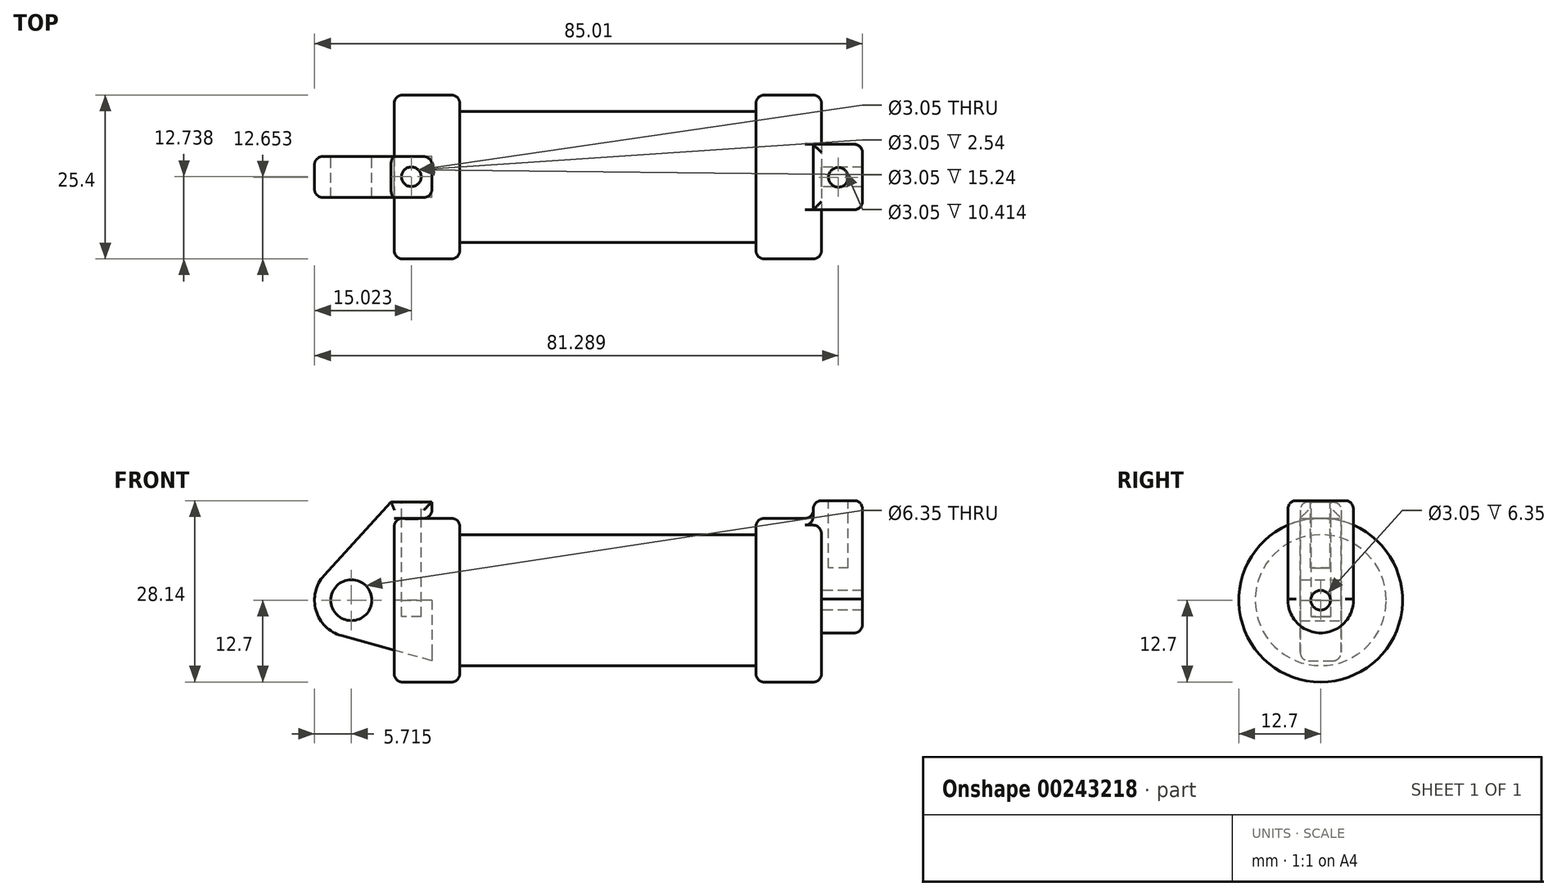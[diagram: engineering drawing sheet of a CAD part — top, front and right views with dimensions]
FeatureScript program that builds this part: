
annotation { "Feature Type Name" : "Feature", "Feature Type Description" : "" }
export const myFeature = defineFeature(function(context is Context, id is Id, definition is map)
    precondition{}
    {
        {
            var Q0;
            Q0=qCreatedBy(makeId("Front.planeOp"),FACE);
            var sketch = newSketch(context, id + "F0", { "sketchPlane" : qUnion([Q0])});
            skLineSegment(sketch, "E0", {"start": v(0, 0) * mm, "end": v(0, 12.7) * mm});
            skLineSegment(sketch, "E1", {"start": v(0, 12.7) * mm, "end": v(10.16, 12.7) * mm});
            skLineSegment(sketch, "E2", {"start": v(10.16, 12.7) * mm, "end": v(10.16, 10.16) * mm});
            skLineSegment(sketch, "E3", {"start": v(10.16, 10.16) * mm, "end": v(56.13, 10.16) * mm});
            skLineSegment(sketch, "E4", {"start": v(56.13, 10.16) * mm, "end": v(56.13, 12.7) * mm});
            skLineSegment(sketch, "E5", {"start": v(56.13, 12.7) * mm, "end": v(66.3, 12.7) * mm});
            skLineSegment(sketch, "E6", {"start": v(66.3, 12.7) * mm, "end": v(66.3, 0) * mm});
            skLineSegment(sketch, "E7", {"start": v(66.3, 0) * mm, "end": v(0, 0) * mm});
            skLineSegment(sketch, "E8", {"start": v(5.84, 15.24) * mm, "end": v(-0.5, 15.24) * mm});
            skLineSegment(sketch, "E9", {"start": v(-0.5, 15.24) * mm, "end": v(-10.88, 3.85) * mm});
            skLineSegment(sketch, "E10", {"start": v(0, 0) * mm, "end": v(-6.65, 0) * mm});
            skCircle(sketch, "E11", {"center": v(-6.65, 0) * mm, "radius": 5.72 * mm});
            skCircle(sketch, "E12", {"center": v(-6.65, 0) * mm, "radius": 3.18 * mm});
            skLineSegment(sketch, "E13", {"start": v(5.84, 15.24) * mm, "end": v(5.84, -9.4) * mm});
            skLineSegment(sketch, "E14", {"start": v(5.84, -9.4) * mm, "end": v(-8.18, -5.5) * mm});
            skSolve(sketch);
        }
        {
            var Q0;
            {var subQ0=sQuery(id+"F0.wireOp",EDGE,"E0");Q0=makeQuery(id+"F0.imprint","IMPRINT",FACE,{"disambiguationData":[TD([[makeQuery(id+"F0.imprint","IMPRINT",EDGE,{"derivedFrom":subQ0}),-1.0]])]});}
            var Q1;
            {var subQ0=sQuery(id+"F0.wireOp",EDGE,"E2");Q1=makeQuery(id+"F0.imprint","IMPRINT",FACE,{"disambiguationData":[TD([[makeQuery(id+"F0.imprint","IMPRINT",EDGE,{"derivedFrom":subQ0}),-1.0]])]});}
            var Q2;
            Q2=sQuery(id+"F0.wireOp",EDGE,"E7");
            revolve(context, id + "F1", {"entities" : qUnion([Q0, Q1]), "axis" : qUnion([Q2]), "revolveType" : RevolveType.FULL});
        }
        {
            var Q0;
            {var subQ3=sQuery(id+"F0.wireOp",EDGE,"E0");Q0=makeQuery(id+"F0.imprint","IMPRINT",FACE,{"disambiguationData":[TD([[makeQuery(id+"F0.imprint","IMPRINT",EDGE,{"derivedFrom":subQ3}),1.0]])]});}
            var Q1;
            {var subQ4=sQuery(id+"F0.wireOp",EDGE,"E12");Q1=makeQuery(id+"F0.imprint","IMPRINT",FACE,{"disambiguationData":[TD([[makeQuery(id+"F0.imprint","IMPRINT",EDGE,{"derivedFrom":subQ4}),-1.0]])]});}
            var Q2;
            {var subQ0=sQuery(id+"F0.wireOp",EDGE,"E14");Q2=makeQuery(id+"F0.imprint","IMPRINT",FACE,{"disambiguationData":[TD([[makeQuery(id+"F0.imprint","IMPRINT",EDGE,{"derivedFrom":subQ0}),-1.0]])]});}
            extrude(context, id + "F2", {"entities" : qUnion([Q0, Q1, Q2]), "endBound" : BoundingType.SYMMETRIC, "depth" : 6.35 * mm});
        }
        {
            var Q0;
            Q0=makeQuery(id+"F1.opRevolve","SWEPT_FACE",FACE,{"disambiguationData":[OSD([sQuery(id+"F0.wireOp",EDGE,"E6")])]});
            var sketch = newSketch(context, id + "F3", { "sketchPlane" : qUnion([Q0])});
            skCircle(sketch, "E15", {"center": v(0, 0) * mm, "radius": 1.52 * mm});
            skCircle(sketch, "E16", {"center": v(0, 0) * mm, "radius": 5.08 * mm});
            skLineSegment(sketch, "E17", {"start": v(-5.08, 0.2) * mm, "end": v(-5.08, 15.44) * mm});
            skLineSegment(sketch, "E18.MirrorCS", {"start": v(5.08, 0.2) * mm, "end": v(5.08, 15.44) * mm});
            skLineSegment(sketch, "E19", {"start": v(-5.08, 15.44) * mm, "end": v(5.19, 15.44) * mm});
            skSolve(sketch);
        }
        {
            var Q0;
            {var subQ0=sQuery(id+"F3.wireOp",EDGE,"E19");var subQ1=sQuery(id+"F3.wireOp",EDGE,"E17");var subQ2=makeQuery(id+"F3.imprint","INTERSECT",VERTEX,{"derivedFrom":[subQ1,subQ0]});Q0=makeQuery(id+"F3.imprint","IMPRINT",FACE,{"disambiguationData":[TD([[makeQuery(id+"F3.imprint","IMPRINT",EDGE,{"disambiguationData":[TD([[subQ2,-1.0]])],"derivedFrom":subQ0}),-1.0]])]});}
            var Q1;
            {var subQ0=sQuery(id+"F3.wireOp",EDGE,"E17");var subQ1=sQuery(id+"F3.wireOp",EDGE,"E16");var subQ2=makeQuery(id+"F3.imprint","INTERSECT",VERTEX,{"derivedFrom":[subQ1,subQ0]});Q1=makeQuery(id+"F3.imprint","IMPRINT",FACE,{"disambiguationData":[TD([[makeQuery(id+"F3.imprint","IMPRINT",EDGE,{"disambiguationData":[TD([[subQ2,1.0]])],"derivedFrom":subQ1}),-1.0]])]});}
            var Q2;
            Q2=makeQuery(id+"F3.imprint","IMPRINT",FACE,{"disambiguationData":[TD([[makeQuery(id+"F3.imprint","IMPRINT",EDGE,{"derivedFrom":sQuery(id+"F3.wireOp",EDGE,"E15")}),-1.0]])]});
            extrude(context, id + "F4", {"entities" : qUnion([Q0, Q1, Q2]), "operationType" : NewBodyOperationType.ADD, "depth" : 6.35 * mm, "hasSecondDirection" : true, "secondDirectionOppositeDirection" : true, "secondDirectionDepth" : 1.27 * mm});
        }
        {
            var Q0;
            Q0=makeQuery(id+"F2.opExtrude","SWEPT_FACE",FACE,{"disambiguationData":[OSD([sQuery(id+"F0.wireOp",EDGE,"E8")])]});
            var sketch = newSketch(context, id + "F5", { "sketchPlane" : qUnion([Q0])});
            skCircle(sketch, "E20", {"center": v(2.65, 0.04) * mm, "radius": 1.52 * mm});
            skCircle(sketch, "E21", {"center": v(68.87, 0.04) * mm, "radius": 1.52 * mm});
            skSolve(sketch);
        }
        {
            var Q0;
            Q0=makeQuery(id+"F5.imprint","IMPRINT",FACE,{"disambiguationData":[TD([[makeQuery(id+"F5.imprint","IMPRINT",EDGE,{"derivedFrom":sQuery(id+"F5.wireOp",EDGE,"E20")}),1.0]])]});
            extrude(context, id + "F6", {"entities" : qUnion([Q0]), "operationType" : NewBodyOperationType.REMOVE, "oppositeDirection" : true, "depth" : 17.78 * mm});
        }
        {
            var Q0;
            Q0=makeQuery(id+"F4.opExtrude","SWEPT_FACE",FACE,{"disambiguationData":[OSD([sQuery(id+"F3.wireOp",EDGE,"E19")])]});
            var sketch = newSketch(context, id + "F7", { "sketchPlane" : qUnion([Q0])});
            skCircle(sketch, "E22", {"center": v(68.92, -0.05) * mm, "radius": 1.52 * mm});
            skSolve(sketch);
        }
        {
            var Q0;
            Q0=makeQuery(id+"F7.imprint","IMPRINT",FACE,{"disambiguationData":[TD([[makeQuery(id+"F7.imprint","IMPRINT",EDGE,{"derivedFrom":sQuery(id+"F7.wireOp",EDGE,"E22")}),1.0]])]});
            extrude(context, id + "F8", {"entities" : qUnion([Q0]), "operationType" : NewBodyOperationType.REMOVE, "oppositeDirection" : true, "depth" : 10.4 * mm});
        }
        {
            var Q0;
            Q0=makeQuery(id+"F4.opExtrude","CAP_EDGE",EDGE,{"disambiguationData":[OSD([sQuery(id+"F3.wireOp",EDGE,"E19")])],"isStart":false});
            var Q1;
            Q1=makeQuery(id+"F4.opExtrude","CAP_EDGE",EDGE,{"disambiguationData":[OSD([sQuery(id+"F3.wireOp",EDGE,"E18.MirrorCS")])],"isStart":false});
            var Q2;
            Q2=makeQuery(id+"F4.opExtrude","CAP_EDGE",EDGE,{"disambiguationData":[OSD([sQuery(id+"F3.wireOp",EDGE,"E16")])],"isStart":false});
            var Q3;
            Q3=makeQuery(id+"F1.opRevolve","SWEPT_EDGE",EDGE,{"disambiguationData":[OSD([sQuery(id+"F0.wireOp",EDGE,"E5"),sQuery(id+"F0.wireOp",EDGE,"E6")])]});
            var Q4;
            Q4=makeQuery(id+"F1.opRevolve","SWEPT_EDGE",EDGE,{"disambiguationData":[OSD([sQuery(id+"F0.wireOp",EDGE,"E4"),sQuery(id+"F0.wireOp",EDGE,"E5")])]});
            var Q5;
            Q5=makeQuery(id+"F1.opRevolve","SWEPT_EDGE",EDGE,{"disambiguationData":[OSD([sQuery(id+"F0.wireOp",EDGE,"E1"),sQuery(id+"F0.wireOp",EDGE,"E2")])]});
            var Q6;
            Q6=makeQuery(id+"F2.opExtrude","CAP_EDGE",EDGE,{"disambiguationData":[OSD([sQuery(id+"F0.wireOp",EDGE,"E8")])],"isStart":true});
            var Q7;
            Q7=makeQuery(id+"F2.opExtrude","CAP_EDGE",EDGE,{"disambiguationData":[OSD([sQuery(id+"F0.wireOp",EDGE,"E9")])],"isStart":true});
            var Q8;
            Q8=makeQuery(id+"F1.opRevolve","SWEPT_EDGE",EDGE,{"disambiguationData":[OSD([sQuery(id+"F0.wireOp",EDGE,"E0"),sQuery(id+"F0.wireOp",EDGE,"E1")])]});
            var Q9;
            Q9=makeQuery(id+"F2.opExtrude","CAP_EDGE",EDGE,{"disambiguationData":[OSD([sQuery(id+"F0.wireOp",EDGE,"E11")])],"isStart":false});
            var Q10;
            Q10=makeQuery(id+"F4.opExtrude","SWEPT_EDGE",EDGE,{"disambiguationData":[OSD([sQuery(id+"F3.wireOp",EDGE,"E18.MirrorCS"),sQuery(id+"F3.wireOp",EDGE,"E19")])]});
            var Q11;
            Q11=makeQuery(id+"F4.opExtrude","CAP_EDGE",EDGE,{"disambiguationData":[OSD([sQuery(id+"F3.wireOp",EDGE,"E19")])],"isStart":true});
            var Q12;
            Q12=makeQuery(id+"F4.opExtrude","SWEPT_EDGE",EDGE,{"disambiguationData":[OSD([sQuery(id+"F3.wireOp",EDGE,"E17"),sQuery(id+"F3.wireOp",EDGE,"E19")])]});
            var Q13;
            Q13=makeQuery(id+"F2.opExtrude","CAP_EDGE",EDGE,{"disambiguationData":[OSD([sQuery(id+"F0.wireOp",EDGE,"E8")])],"isStart":false});
            var Q14;
            {var subQ0=sQuery(id+"F0.wireOp",EDGE,"E13");Q14=makeQuery(id+"F2.opExtrude","CAP_EDGE",EDGE,{"disambiguationData":[OSD([subQ0]),TDD([makeQuery(id+"F0.imprint","IMPRINT",EDGE,{"disambiguationData":[TD([[makeQuery(id+"F0.imprint","INTERSECT",VERTEX,{"derivedFrom":[sQuery(id+"F0.wireOp",EDGE,"E8"),subQ0]}),-1.0]])],"derivedFrom":subQ0})])],"isStart":false});}
            var Q15;
            {var subQ0=sQuery(id+"F0.wireOp",EDGE,"E13");Q15=makeQuery(id+"F2.opExtrude","CAP_EDGE",EDGE,{"disambiguationData":[OSD([subQ0]),TDD([makeQuery(id+"F0.imprint","IMPRINT",EDGE,{"disambiguationData":[TD([[makeQuery(id+"F0.imprint","INTERSECT",VERTEX,{"derivedFrom":[sQuery(id+"F0.wireOp",EDGE,"E8"),subQ0]}),-1.0]])],"derivedFrom":subQ0})])],"isStart":true});}
            var Q16;
            Q16=makeQuery(id+"F4.boolean.opBoolean","INTERSECT",EDGE,{"derivedFrom":[makeQuery(id+"F1.opRevolve","SWEPT_FACE",FACE,{"disambiguationData":[OSD([sQuery(id+"F0.wireOp",EDGE,"E5")])]}),makeQuery(id+"F4.opExtrude","CAP_FACE",FACE,{"disambiguationData":[OSD([sQuery(id+"F3.wireOp",EDGE,"E15"),sQuery(id+"F3.wireOp",EDGE,"E16"),sQuery(id+"F3.wireOp",EDGE,"E17"),sQuery(id+"F3.wireOp",EDGE,"E18.MirrorCS"),sQuery(id+"F3.wireOp",EDGE,"E19")])],"isStart":true})]});
            var Q17;
            Q17=makeQuery(id+"F2.opExtrude","SWEPT_EDGE",EDGE,{"disambiguationData":[OSD([sQuery(id+"F0.wireOp",EDGE,"E1"),sQuery(id+"F0.wireOp",EDGE,"E13")])]});
            fillet(context, id + "F9", {"entities" : qUnion([Q0, Q1, Q2, Q3, Q4, Q5, Q6, Q7, Q8, Q9, Q10, Q11, Q12, Q13, Q14, Q15, Q16, Q17]), "radius" : 1.27 * mm, "tangentPropagation" : true, "allowEdgeOverflow" : false});
        }
    });
